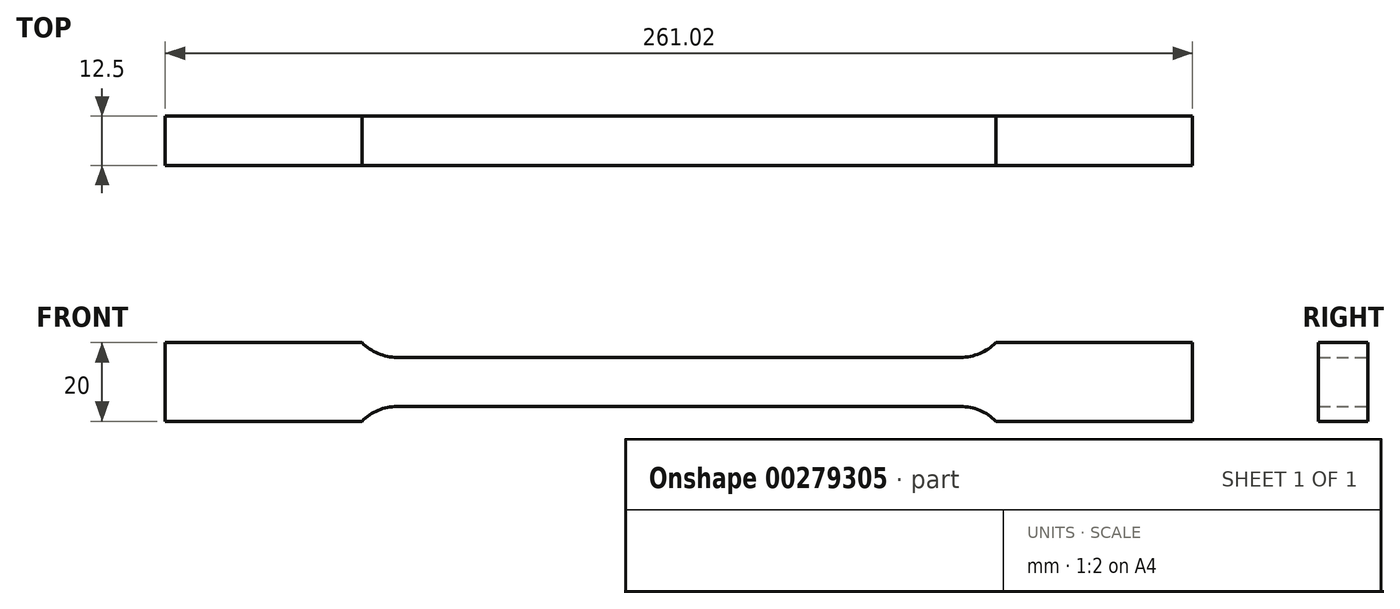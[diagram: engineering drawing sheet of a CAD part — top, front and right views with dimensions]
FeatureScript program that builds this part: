
annotation { "Feature Type Name" : "Feature", "Feature Type Description" : "" }
export const myFeature = defineFeature(function(context is Context, id is Id, definition is map)
    precondition{}
    {
        {
            var Q0;
            Q0=qCreatedBy(makeId("Front.planeOp"),FACE);
            var sketch = newSketch(context, id + "F0", { "sketchPlane" : qUnion([Q0])});
            skLineSegment(sketch, "E0", {"start": v(0, 6.25) * mm, "end": v(71.58, 6.25) * mm});
            skArc(sketch, "E1", {"start": v(71.58, 6.25) * mm, "mid": v(76.42, 7.23) * mm, "end": v(80.5, 10) * mm});
            skLineSegment(sketch, "E2", {"start": v(80.5, 10) * mm, "end": v(130.5, 10) * mm});
            skLineSegment(sketch, "E3", {"start": v(130.5, 10) * mm, "end": v(130.5, 0) * mm});
            skLineSegment(sketch, "E4.MirrorCS", {"start": v(0, -6.25) * mm, "end": v(71.58, -6.25) * mm});
            skLineSegment(sketch, "E5.MirrorCS", {"start": v(130.5, -10) * mm, "end": v(130.5, 0) * mm});
            skLineSegment(sketch, "E6.MirrorCS", {"start": v(80.5, -10) * mm, "end": v(130.5, -10) * mm});
            skArc(sketch, "E7.MirrorCS", {"start": v(71.58, -6.25) * mm, "mid": v(76.42, -7.23) * mm, "end": v(80.5, -10) * mm});
            skArc(sketch, "E8.MirrorCS", {"start": v(-71.58, -6.25) * mm, "mid": v(-76.42, -7.23) * mm, "end": v(-80.5, -10) * mm});
            skLineSegment(sketch, "E9.MirrorCS", {"start": v(-80.5, -10) * mm, "end": v(-130.5, -10) * mm});
            skArc(sketch, "E10.MirrorCS", {"start": v(-71.58, 6.25) * mm, "mid": v(-76.42, 7.23) * mm, "end": v(-80.5, 10) * mm});
            skLineSegment(sketch, "E11.MirrorCS", {"start": v(-80.5, 10) * mm, "end": v(-130.5, 10) * mm});
            skLineSegment(sketch, "E12.MirrorCS", {"start": v(-130.5, -10) * mm, "end": v(-130.5, 0) * mm});
            skLineSegment(sketch, "E13.MirrorCS", {"start": v(0, -6.25) * mm, "end": v(-71.58, -6.25) * mm});
            skLineSegment(sketch, "E14.MirrorCS", {"start": v(-130.5, 10) * mm, "end": v(-130.5, 0) * mm});
            skLineSegment(sketch, "E15.MirrorCS", {"start": v(0, 6.25) * mm, "end": v(-71.58, 6.25) * mm});
            skSolve(sketch);
        }
        {
            var Q0;
            Q0 = qSketchRegion(id + "F0", true);
            extrude(context, id + "F1", {"entities" : qUnion([Q0]), "endBound" : BoundingType.SYMMETRIC, "depth" : 12.5 * mm});
        }
    });
